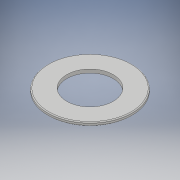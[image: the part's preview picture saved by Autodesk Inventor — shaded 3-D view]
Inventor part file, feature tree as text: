
AUTODESK INVENTOR PART (.ipt)
format: ipt  version: 2018 (Build 220112000, 112)  size: 116,736 bytes
history: native  units: mm
features: extrude x1, fillet x1, sketch x1
ambient origin geometry x8: Origin, YZ Plane, XZ Plane, XY Plane, X Axis, Y Axis, Z Axis, Center Point
bodies: Solid1 (feature_tree)
feature tree (3):
  extrude  "Extrusion1"  Depth=0.2mm
  fillet  "Fillet1"  Radius=0.8mm
  sketch  "Sketch1"  dims[d0=10.5mm d1=19.0mm d2=0.8mm d3=0.0mm d4=0.2mm]
